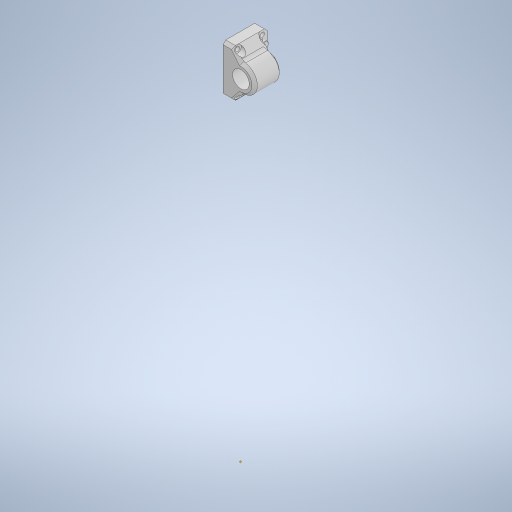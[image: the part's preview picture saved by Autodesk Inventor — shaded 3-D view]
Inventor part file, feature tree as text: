
AUTODESK INVENTOR PART (.ipt)
format: ipt  version: 2024.1 (Build 281209000, 209)  size: 633,344 bytes
history: native  units: mm
features: extrude x12, sketch x12, chamfer x9, other x7, projected_geometry x3, plane x2, fillet x2, reference x2
ambient origin geometry x8: Origin, YZ Plane, XZ Plane, XY Plane, X Axis, Y Axis, Z Axis, Center Point
bodies: Body1 (feature_tree), Body2 (feature_tree), Body3 (feature_tree)
feature tree (49):
  other  "clamp-top"
  plane  "Work Plane1"
  plane  "Work Plane2"
  extrude  "Extrusion1"  Depth=7.5mm
  extrude  "Extrusion2"  Depth=35.0mm TaperAngle=0.0deg
  extrude  "Extrusion3"  Depth=12.3mm
  chamfer  "Chamfer2"  Distance=30.0mm
  extrude  "Extrusion4"  Depth=4.7mm
  chamfer  "Chamfer3"  Distance=2.0mm Angle=45.0deg
  extrude  "Extrusion5"  Depth=3.2mm
  chamfer  "Chamfer4"  Distance=3.0mm
  extrude  "Extrusion7"  Depth=10.0mm
  extrude  "Extrusion6"  Depth=10.0mm
  fillet  "Fillet1"  [1 undecoded]
  chamfer  "Chamfer9"  Distance=5.45mm
  chamfer  "Chamfer10"  Distance=10.0mm
  extrude  "Extrusion8"  Depth=10.0mm TaperAngle=45.0deg
  chamfer  "Chamfer11"  Distance=6.0mm
  chamfer  "Chamfer12"  Distance=3.5mm
  extrude  "Extrusion9"  Depth=10.0mm TaperAngle=45.0deg
  extrude  "Extrusion10"  Depth=10.0mm
  extrude  "Extrusion11"  Depth=10.0mm TaperAngle=0.0deg
  chamfer  "Chamfer13"  Distance=0.3mm
  fillet  "Fillet2"  Radius=1.0mm
  extrude  "Extrusion12"  Depth=10.0mm TaperAngle=45.0deg
  chamfer  "Chamfer1"  Distance=1.2mm Angle=45.0deg
  other  "Work Point1"
  sketch  "Sketch2"  dims[d0=7.5mm d1=7.5mm]
  reference  "Reference1"
  sketch  "Sketch3"  dims[d2=2.0mm d3=35.0mm d4=0.0mm]
  sketch  "Sketch4"  dims[d5=0.25mm d6=12.3mm]
  projected_geometry  "Projected Loop1"
  projected_geometry  "Projected Loop2"
  projected_geometry  "Projected Loop3"
  sketch  "Sketch5"  dims[d7=6.0mm]
  sketch  "Sketch6"  dims[d9=4.0mm d10=30.0mm d11=0.0mm]
  sketch  "Sketch7"  dims[d12=0.0mm d13=0.0mm d14=4.7mm]
  other  "screw-cap"
  sketch  "Sketch8"  dims[d15=4.7mm d16=2.0mm d17=2.0mm d18=45.0deg]
  sketch  "Sketch9"  dims[d19=3.0mm d20=2.0mm d21=45.0deg d22=3.2mm]
  reference  "Reference2"
  other  "clamp-base"
  sketch  "Sketch10"  dims[d23=3.0mm]
  sketch  "Sketch11"  dims[d24=3.0mm]
  sketch  "Sketch12"  dims[d25=6.0mm]
  sketch  "Sketch13"  dims[d26=6.0mm d27=3.0mm d28=3.0mm d29=3.5mm d31=0.0mm d32=0.0mm d33=5.45mm d34=10.0mm d35=0.0mm d36=2.0mm d37=2.0mm d38=45.0deg d39=6.0mm d40=3.5mm d41=2.0mm d42=2.0mm d43=45.0deg d47=5.35mm d48=3.0mm d49=0.0mm d50=0.3mm d51=1.0mm d52=0.0mm d62=2.0mm d63=2.0mm d64=45.0deg d65=1.2mm d66=2.0mm d67=45.0deg d68=0.5mm d69=8.0mm d70=1.0mm d71=0.0mm d72=2.0mm d73=2.0mm d74=45.0deg d75=2.0mm d76=2.0mm d77=45.0deg d78=0.0mm d79=0.0mm d80=4.92mm d81=10.0mm d82=0.0mm d83=35.0mm d84=17.5mm d85=0.0mm d86=0.0mm d87=2.0mm d88=2.0mm d89=45.0deg d90=4.0mm d91=10.0mm d92=0.0mm]
  other  "<userpath>\Documents\0004-CAD\3D-cad-main\bike-rack\bike-rack-assembly.iam"
  other  "bike-rack-assembly.iam"
  other  "bike-rack:1"
note: 1 required parameter value undecoded (feature->parameter linkage not recoverable at this tier; creation-order binding heuristic only, values carry confidence <= 0.55)
